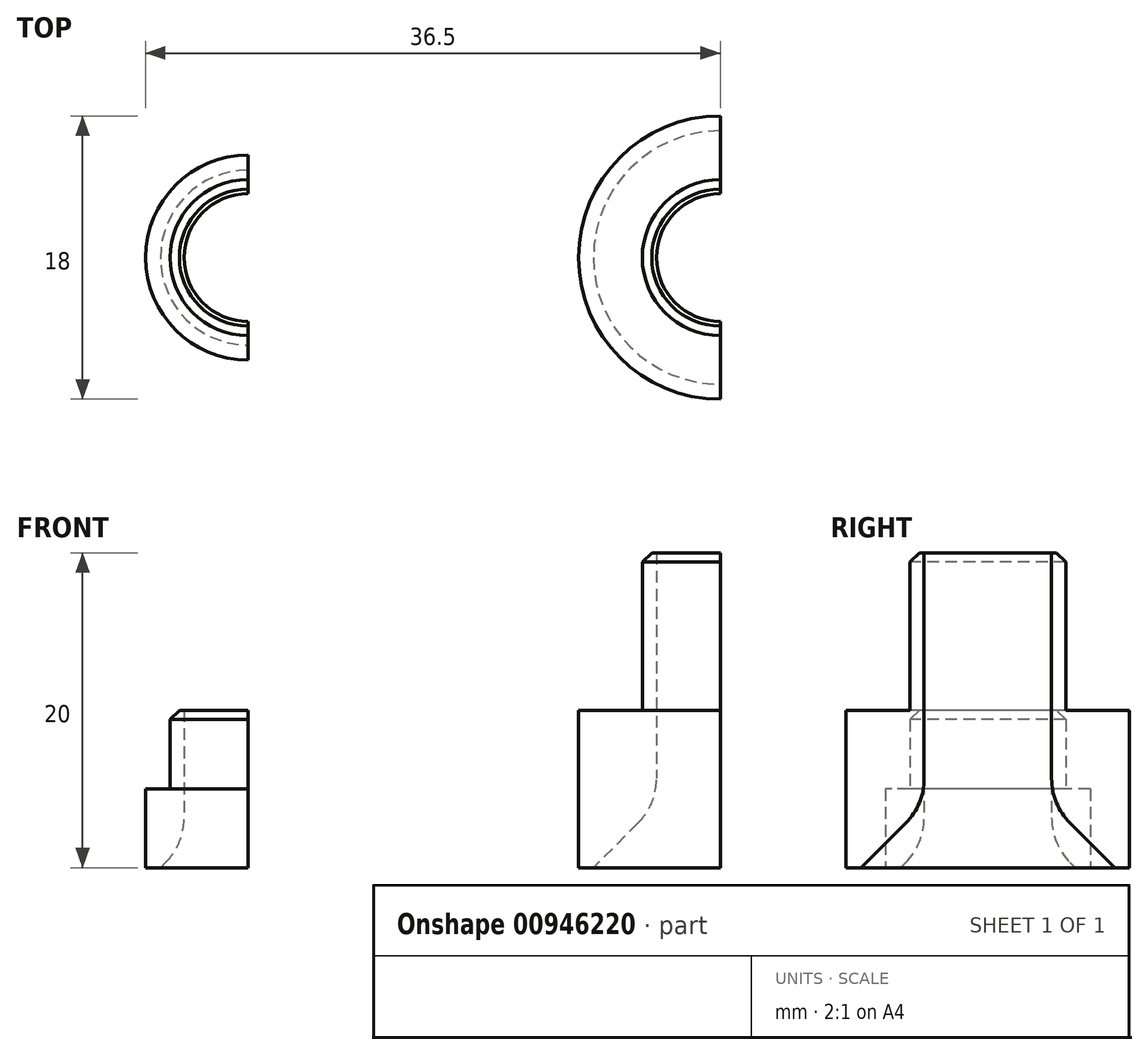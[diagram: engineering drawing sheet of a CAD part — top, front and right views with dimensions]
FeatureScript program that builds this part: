
annotation { "Feature Type Name" : "Feature", "Feature Type Description" : "" }
export const myFeature = defineFeature(function(context is Context, id is Id, definition is map)
    precondition{}
    {
        {
            var Q0;
            Q0=qCreatedBy(makeId("Top.planeOp"),FACE);
            var sketch = newSketch(context, id + "F0", { "sketchPlane" : qUnion([Q0])});
            skArc(sketch, "E0", {"start": v(0, 6.5) * mm, "mid": v(-6.5, 0) * mm, "end": v(0, -6.5) * mm});
            skArc(sketch, "E1", {"start": v(0, 4.95) * mm, "mid": v(-4.95, 0) * mm, "end": v(0, -4.95) * mm});
            skArc(sketch, "E2", {"start": v(0, 4.05) * mm, "mid": v(-4.05, 0) * mm, "end": v(0, -4.05) * mm});
            skLineSegment(sketch, "E3", {"start": v(0, 6.5) * mm, "end": v(0, 4.05) * mm});
            skLineSegment(sketch, "E4.trimOffspring", {"start": v(0, -4.05) * mm, "end": v(0, -6.5) * mm});
            skArc(sketch, "E5", {"start": v(30, 9) * mm, "mid": v(21, 0) * mm, "end": v(30, -9) * mm});
            skArc(sketch, "E6", {"start": v(30, 4.95) * mm, "mid": v(25.05, 0) * mm, "end": v(30, -4.95) * mm});
            skArc(sketch, "E7", {"start": v(30, 4.05) * mm, "mid": v(25.95, 0) * mm, "end": v(30, -4.05) * mm});
            skLineSegment(sketch, "E8", {"start": v(30, 9) * mm, "end": v(30, -9) * mm});
            skSolve(sketch);
        }
        {
            var Q0;
            {var subQ0=sQuery(id+"F0.wireOp",EDGE,"E0");Q0=makeQuery(id+"F0.imprint","IMPRINT",FACE,{"disambiguationData":[TD([[makeQuery(id+"F0.imprint","IMPRINT",EDGE,{"derivedFrom":subQ0}),1.0]])]});}
            extrude(context, id + "F1", {"entities" : qUnion([Q0]), "depth" : 5 * mm, "offsetDistance" : 25 * mm});
        }
        {
            var Q0;
            {var subQ0=sQuery(id+"F0.wireOp",EDGE,"E1");Q0=makeQuery(id+"F0.imprint","IMPRINT",FACE,{"disambiguationData":[TD([[makeQuery(id+"F0.imprint","IMPRINT",EDGE,{"derivedFrom":subQ0}),1.0]])]});}
            extrude(context, id + "F2", {"entities" : qUnion([Q0]), "operationType" : NewBodyOperationType.ADD, "depth" : 10 * mm, "offsetDistance" : 25 * mm});
        }
        {
            var Q0;
            Q0=makeQuery(id+"F0.imprint","IMPRINT",FACE,{"disambiguationData":[TD([[makeQuery(id+"F0.imprint","IMPRINT",EDGE,{"derivedFrom":sQuery(id+"F0.wireOp",EDGE,"E5")}),1.0]])]});
            extrude(context, id + "F3", {"entities" : qUnion([Q0]), "depth" : 10 * mm, "offsetDistance" : 25 * mm});
        }
        {
            var Q0;
            Q0=makeQuery(id+"F0.imprint","IMPRINT",FACE,{"disambiguationData":[TD([[makeQuery(id+"F0.imprint","IMPRINT",EDGE,{"derivedFrom":sQuery(id+"F0.wireOp",EDGE,"E6")}),1.0]])]});
            extrude(context, id + "F4", {"entities" : qUnion([Q0]), "operationType" : NewBodyOperationType.ADD, "depth" : 20 * mm, "offsetDistance" : 25 * mm});
        }
        {
            var Q0;
            Q0=makeQuery(id+"F2.opExtrude","CAP_EDGE",EDGE,{"disambiguationData":[OSD([sQuery(id+"F0.wireOp",EDGE,"E2")])],"isStart":true});
            chamfer(context, id + "F5", {"entities" : qUnion([Q0]), "width" : 1.5 * mm, "tangentPropagation" : true});
        }
        {
            var Q0;
            Q0=makeQuery(id+"F2.opExtrude","CAP_EDGE",EDGE,{"disambiguationData":[OSD([sQuery(id+"F0.wireOp",EDGE,"E1")])],"isStart":false});
            var Q1;
            Q1=makeQuery(id+"F4.opExtrude","CAP_EDGE",EDGE,{"disambiguationData":[OSD([sQuery(id+"F0.wireOp",EDGE,"E6")])],"isStart":false});
            chamfer(context, id + "F6", {"entities" : qUnion([Q0, Q1]), "width" : 0.6 * mm, "tangentPropagation" : true});
        }
        {
            var Q0;
            Q0=makeQuery(id+"F4.opExtrude","CAP_EDGE",EDGE,{"disambiguationData":[OSD([sQuery(id+"F0.wireOp",EDGE,"E7")])],"isStart":true});
            chamfer(context, id + "F7", {"entities" : qUnion([Q0]), "width" : 4 * mm, "tangentPropagation" : true});
        }
        {
            var Q0;
            {var subQ0=sQuery(id+"F0.wireOp",EDGE,"E2");Q0=makeQuery(id+"F5.opChamfer","BLEND_EDGE",EDGE,{"blendedFrom":[makeQuery(id+"F2.opExtrude","CAP_EDGE",EDGE,{"disambiguationData":[OSD([subQ0])],"isStart":true}),makeQuery(id+"F2.opExtrude","SWEPT_FACE",FACE,{"disambiguationData":[OSD([subQ0])]})],"blendedInto":[makeQuery(id+"F2.opExtrude","SWEPT_FACE",FACE,{"disambiguationData":[OSD([subQ0])]})]});}
            var Q1;
            {var subQ0=sQuery(id+"F0.wireOp",EDGE,"E7");Q1=makeQuery(id+"F7.opChamfer","BLEND_EDGE",EDGE,{"blendedFrom":[makeQuery(id+"F4.opExtrude","CAP_EDGE",EDGE,{"disambiguationData":[OSD([subQ0])],"isStart":true}),makeQuery(id+"F4.opExtrude","SWEPT_FACE",FACE,{"disambiguationData":[OSD([subQ0])]})],"blendedInto":[makeQuery(id+"F4.opExtrude","SWEPT_FACE",FACE,{"disambiguationData":[OSD([subQ0])]})]});}
            fillet(context, id + "F8", {"entities" : qUnion([Q0, Q1]), "radius" : 4 * mm, "tangentPropagation" : true, "allowEdgeOverflow" : false});
        }
    });
